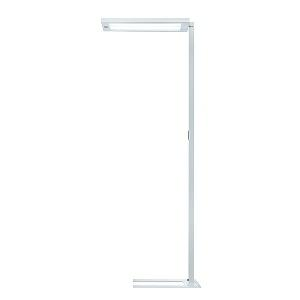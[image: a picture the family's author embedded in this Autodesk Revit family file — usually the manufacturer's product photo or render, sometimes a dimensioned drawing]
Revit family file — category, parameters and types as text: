
# Revit family: lavigo_-_dps_6000_840_r_g2_00803392_7a24
name_source: partatom
category: Lighting Fixtures
units: mm (PartAtom-declared; Revit-internal decimal feet)

## family parameters
Cut with Voids When Loaded = No
Host = Face
Light Source = No
Part Type = Normal
Room Calculation Point = No
Round Connector Dimension = Use Diameter
Shared = No

## types (1)
- LAVIGO - DPS 6000/840/R/G2 (1 x LED, 5950 lm, 4000K)
    Apparent Load = 45 VA
    Approval mark = CE
    CIE Flux Codes = 60 87 97 29 100
    Color Rendering = 80-89
    Color Temperature = 4000K
    Control Gear = Electronic ballast
    Default Elevation = 1800 mm
    Description = DPS 6000/840/R/G2|Free-standing luminaire|light source: LED|work equipment: Electronic ballast|connected load: 220-240 V, 50/60 Hz|Power consumption: approx. 45 W|standby: approx. 0,50|power factor: approx. 0,865|luminous flux: 5950 lm|luminous efficacy: 132 lm/W|light distribution: Direct/indirect|direct ratio: approx. 29 %|colour temperature: Cold white, ca. 4000 K|color rendering index (CRI): >= 80|chromaticity tolerance:  3 SDCM|technology: Presence and daylight sensor control (PIR)|operation: Multi-function switch|luminaire body|material: Steel/plastic|surface: Painted|colour: White|lamp cover: Acrylic (PMMA), Satine|tubular section|material: Steel tube|surface: Painted|Form: Tubular section upright|colour of tubular section: White|luminaire base|Form: C-form flat|weight (net): approx. 19.7 kg|mains lead: 3.00 m Mains plug CEE 7/VII|Fastening: Floor standing base|decorative contrast side parts: Flint grey|glare control: Prism aperture|luminance(L65): <= 3000 cd/m|unified glare rating(4H 8H): <=  16|special features: Luminaire head detachable, Cradle to Cradle Certified TM, Direct light component with edge light and light-guide technology for homogenous light exit, Flicker-free, Integrated light and presence sensor PIR, Retrofittable with TALK module, Separated, direct and indirect light individually adjustable|
    Frequency = 50 Hz
    Height = 36 mm
    Lamp = 1 x LED
    Lamp Light Flux = 5950 lm
    Lamp count = 1
    Length = 675 mm
    Luminous efficacy = 132 lm/W
    Manufacturer = Waldmann
    ModVariant = No
    Model = 00803392
    Mounting Place = Floor
    Mounting Type = Freestanding
    Number of Poles = 1
    OnlyDefault = Yes
    Power Factor = 1
    Product Name = LAVIGO - DPS 6000/840/R/G2
    Product group = Free standing luminaire
    ProductGroupID = 13
    Protection Class = Protection class I
    Protection Degree = IP 20
    RLX_Detail_Level = 1
    RLX_Emergency_Light_Flux = 0 lm
    RLX_Emergency_Type = 0
    RLX_Emergency_Type_DB = No
    RlxData = <blob elided: 37865 chars, md5=a8beea36>
    Socket = socket
    Standby Power = 0 W
    System Light Flux = 5950 lm
    System Power = 45 W
    Type Comments = Product without accessories
    Type Image = 121695000-00610208.jpg
    URL = http://relux.com
    VarID = ---
    Voltage = 230 V
    Voltage Range = 220-240 V
    Weight = 0.00 kg
    Width = 320 mm

## geometry (parser evidence)
native form markers: Blend x4, Sweep x14
no freeform markers — native parametric forms only
